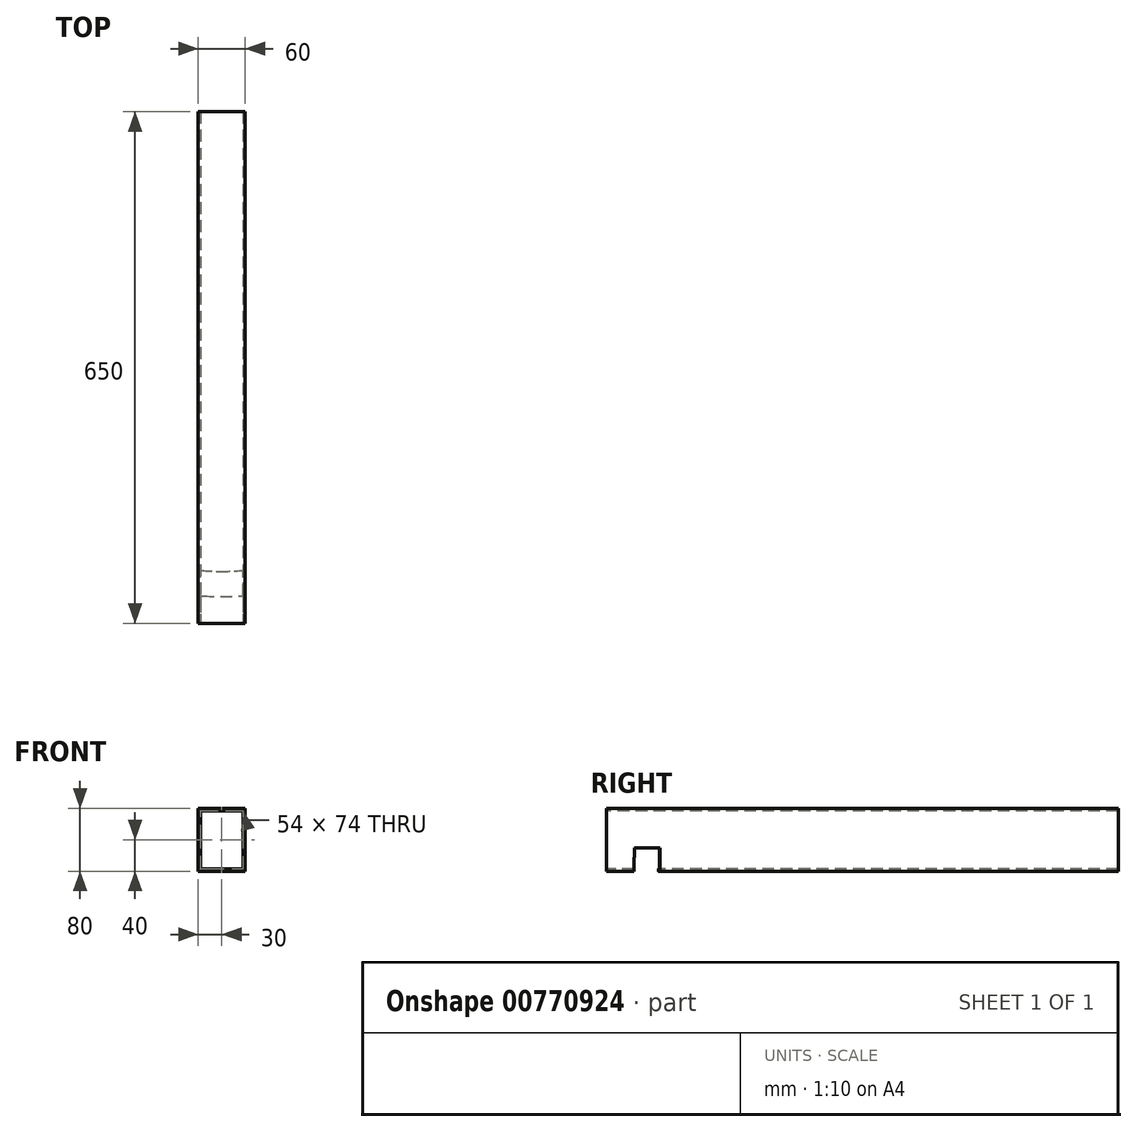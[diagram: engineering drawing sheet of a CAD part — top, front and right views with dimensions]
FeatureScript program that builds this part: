
annotation { "Feature Type Name" : "Feature", "Feature Type Description" : "" }
export const myFeature = defineFeature(function(context is Context, id is Id, definition is map)
    precondition{}
    {
        {
            var Q0;
            Q0=qCreatedBy(makeId("Front.planeOp"),FACE);
            var sketch = newSketch(context, id + "F0", { "sketchPlane" : qUnion([Q0])});
            skLineSegment(sketch, "E0.bottom", {"start": v(30, -30) * mm, "end": v(-30, -30) * mm});
            skLineSegment(sketch, "E0.top", {"start": v(30, 50) * mm, "end": v(-30, 50) * mm});
            skLineSegment(sketch, "E0.left", {"start": v(30, -30) * mm, "end": v(30, 50) * mm});
            skLineSegment(sketch, "E0.right", {"start": v(-30, -30) * mm, "end": v(-30, 50) * mm});
            skLineSegment(sketch, "E1.0", {"start": v(27, 47) * mm, "end": v(-27, 47) * mm});
            skLineSegment(sketch, "E1.1", {"start": v(27, -27) * mm, "end": v(27, 47) * mm});
            skLineSegment(sketch, "E1.2", {"start": v(27, -27) * mm, "end": v(-27, -27) * mm});
            skLineSegment(sketch, "E1.3", {"start": v(-27, -27) * mm, "end": v(-27, 47) * mm});
            skSolve(sketch);
        }
        {
            var Q0;
            Q0 = qSketchRegion(id + "F0", true);
            extrude(context, id + "F1", {"entities" : qUnion([Q0]), "oppositeDirection" : true, "depth" : 600 * mm, "offsetDistance" : 25 * mm, "hasSecondDirection" : true, "secondDirectionOppositeDirection" : false, "secondDirectionDepth" : 50 * mm});
        }
        {
            var Q0;
            Q0=qCreatedBy(makeId("Right.planeOp"),FACE);
            var sketch = newSketch(context, id + "F2", { "sketchPlane" : qUnion([Q0])});
            skArc(sketch, "E2", {"start": v(15, -15) * mm, "mid": v(0, 0) * mm, "end": v(-15, -15) * mm});
            skLineSegment(sketch, "E3", {"start": v(-15, -15) * mm, "end": v(-15, -30) * mm});
            skLineSegment(sketch, "E4", {"start": v(-15, -30) * mm, "end": v(15, -30) * mm});
            skLineSegment(sketch, "E5", {"start": v(15, -30) * mm, "end": v(15, -15) * mm});
            skSolve(sketch);
        }
        {
            var Q0;
            Q0 = qSketchRegion(id + "F2", true);
            extrude(context, id + "F3", {"entities" : qUnion([Q0]), "operationType" : NewBodyOperationType.REMOVE, "endBound" : BoundingType.THROUGH_ALL, "oppositeDirection" : true, "depth" : 25 * mm, "offsetDistance" : 25 * mm, "hasSecondDirection" : true, "secondDirectionBound" : SecondDirectionBoundingType.THROUGH_ALL, "secondDirectionOppositeDirection" : false, "secondDirectionDepth" : 25 * mm});
        }
        {
            var Q0;
            {var subQ2=sQuery(id+"F0.wireOp",EDGE,"E0.bottom");Q0=makeQuery(id+"F3.boolean.opBoolean","SPLIT",FACE,{"disambiguationData":[TD([makeQuery(id+"F3.opExtrude","SWEPT_FACE",FACE,{"disambiguationData":[OSD([sQuery(id+"F2.wireOp",EDGE,"E5")])]})])],"derivedFrom":makeQuery(id+"F1.opExtrude","SWEPT_FACE",FACE,{"disambiguationData":[OSD([subQ2])]})});}
            var sketch = newSketch(context, id + "F4", { "sketchPlane" : qUnion([Q0])});
            skArc(sketch, "E6", {"start": v(30, 14.5) * mm, "mid": v(0, 16) * mm, "end": v(-30, 14.5) * mm});
            skArc(sketch, "E7.0", {"start": v(30, -17.68) * mm, "mid": v(0, -16) * mm, "end": v(-30, -17.68) * mm});
            skLineSegment(sketch, "E8", {"start": v(-30, 14.5) * mm, "end": v(-30, -17.68) * mm});
            skLineSegment(sketch, "E9", {"start": v(30, 14.5) * mm, "end": v(30, -17.68) * mm});
            skSolve(sketch);
        }
        {
            var Q0;
            Q0 = qSketchRegion(id + "F4", true);
            extrude(context, id + "F5", {"entities" : qUnion([Q0]), "operationType" : NewBodyOperationType.REMOVE, "oppositeDirection" : true, "depth" : 30 * mm, "offsetDistance" : 25 * mm});
        }
    });
